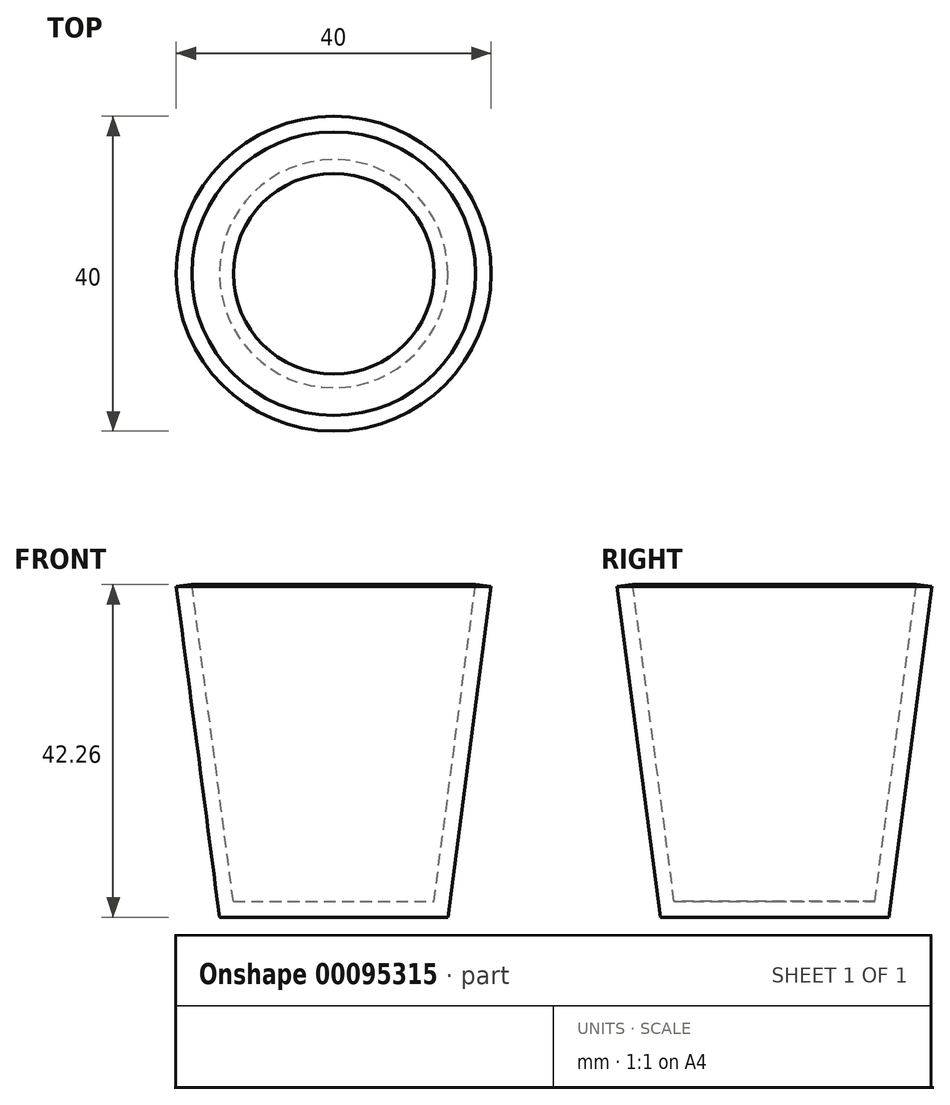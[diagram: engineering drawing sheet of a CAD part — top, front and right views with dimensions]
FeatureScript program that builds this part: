
annotation { "Feature Type Name" : "Feature", "Feature Type Description" : "" }
export const myFeature = defineFeature(function(context is Context, id is Id, definition is map)
    precondition{}
    {
        {
            var Q0;
            Q0=qCreatedBy(makeId("Front.planeOp"),FACE);
            var sketch = newSketch(context, id + "F0", { "sketchPlane" : qUnion([Q0])});
            skLineSegment(sketch, "E0", {"start": v(0, -19.42) * mm, "end": v(-14.5, -19.42) * mm});
            skLineSegment(sketch, "E1", {"start": v(-20, 22.58) * mm, "end": v(-14.5, -19.42) * mm});
            skLineSegment(sketch, "E2.0", {"start": v(0, -17.42) * mm, "end": v(-12.74, -17.42) * mm});
            skLineSegment(sketch, "E2.1", {"start": v(-18.02, 22.84) * mm, "end": v(-12.74, -17.42) * mm});
            skLineSegment(sketch, "E3", {"start": v(-20, 22.58) * mm, "end": v(-18.02, 22.84) * mm});
            skLineSegment(sketch, "E4", {"start": v(0, -17.42) * mm, "end": v(0, -19.42) * mm});
            skLineSegment(sketch, "E5.bottom", {"start": v(0, -17.42) * mm, "end": v(-2.5, -17.42) * mm});
            skLineSegment(sketch, "E5.top", {"start": v(0, 35.58) * mm, "end": v(-2.5, 35.58) * mm});
            skLineSegment(sketch, "E5.left", {"start": v(0, -17.42) * mm, "end": v(0, 35.58) * mm});
            skLineSegment(sketch, "E5.right", {"start": v(-2.5, -17.42) * mm, "end": v(-2.5, 35.58) * mm});
            skSolve(sketch);
        }
        {
            var Q0;
            Q0=makeQuery(id+"F0.imprint","IMPRINT",FACE,{"disambiguationData":[TD([[makeQuery(id+"F0.imprint","IMPRINT",EDGE,{"derivedFrom":sQuery(id+"F0.wireOp",EDGE,"E0")}),-1.0]])]});
            var Q1;
            Q1=makeQuery(id+"F0.imprint","IMPRINT",FACE,{"disambiguationData":[TD([[makeQuery(id+"F0.imprint","IMPRINT",EDGE,{"derivedFrom":sQuery(id+"F0.wireOp",EDGE,"E5.bottom")}),-1.0]])]});
            var Q2;
            Q2=sQuery(id+"F0.wireOp",EDGE,"E5.left");
            revolve(context, id + "F1", {"entities" : qUnion([Q0, Q1]), "axis" : qUnion([Q2]), "revolveType" : RevolveType.FULL});
        }
    });
